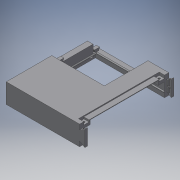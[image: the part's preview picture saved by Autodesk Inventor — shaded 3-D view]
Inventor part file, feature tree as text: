
AUTODESK INVENTOR PART (.ipt)
format: ipt  version: 2016 SP2 (Build 200236200, 236)  size: 869,376 bytes
history: native  units: mm
features: sketch x26, other x5
ambient origin geometry x8: Origin, YZ Plane, XZ Plane, XY Plane, X Axis, Y Axis, Z Axis, Center Point
bodies: Volumenkörper1 (feature_tree), Volumenkörper2 (feature_tree), Volumenkörper3 (feature_tree)
feature tree (31):
  other  "Case_side_back.ipt"
  other  "Volumenkörper1::Case_side_back.ipt"
  other  "Volumenkörper4::Case_side_back.ipt"
  other  "Volumenkörper5::Case_side_back.ipt"
  other  "Bezeichnung1"
  sketch  "Skizze1"  dims[d0=10.0mm]
  sketch  "Skizze2"
  sketch  "Skizze3"
  sketch  "Skizze4"
  sketch  "Skizze6"
  sketch  "Skizze9"
  sketch  "Skizze10"
  sketch  "Skizze11"
  sketch  "Skizze12"
  sketch  "Skizze13"
  sketch  "Skizze14"
  sketch  "Skizze15"
  sketch  "Skizze16"
  sketch  "Skizze17"
  sketch  "Skizze18"
  sketch  "Skizze19"
  sketch  "Skizze20"
  sketch  "Skizze21"
  sketch  "Skizze22"
  sketch  "Skizze27"
  sketch  "Skizze28"
  sketch  "Skizze29"
  sketch  "Skizze30"
  sketch  "Skizze31"
  sketch  "Skizze32"
  sketch  "Skizze33"
